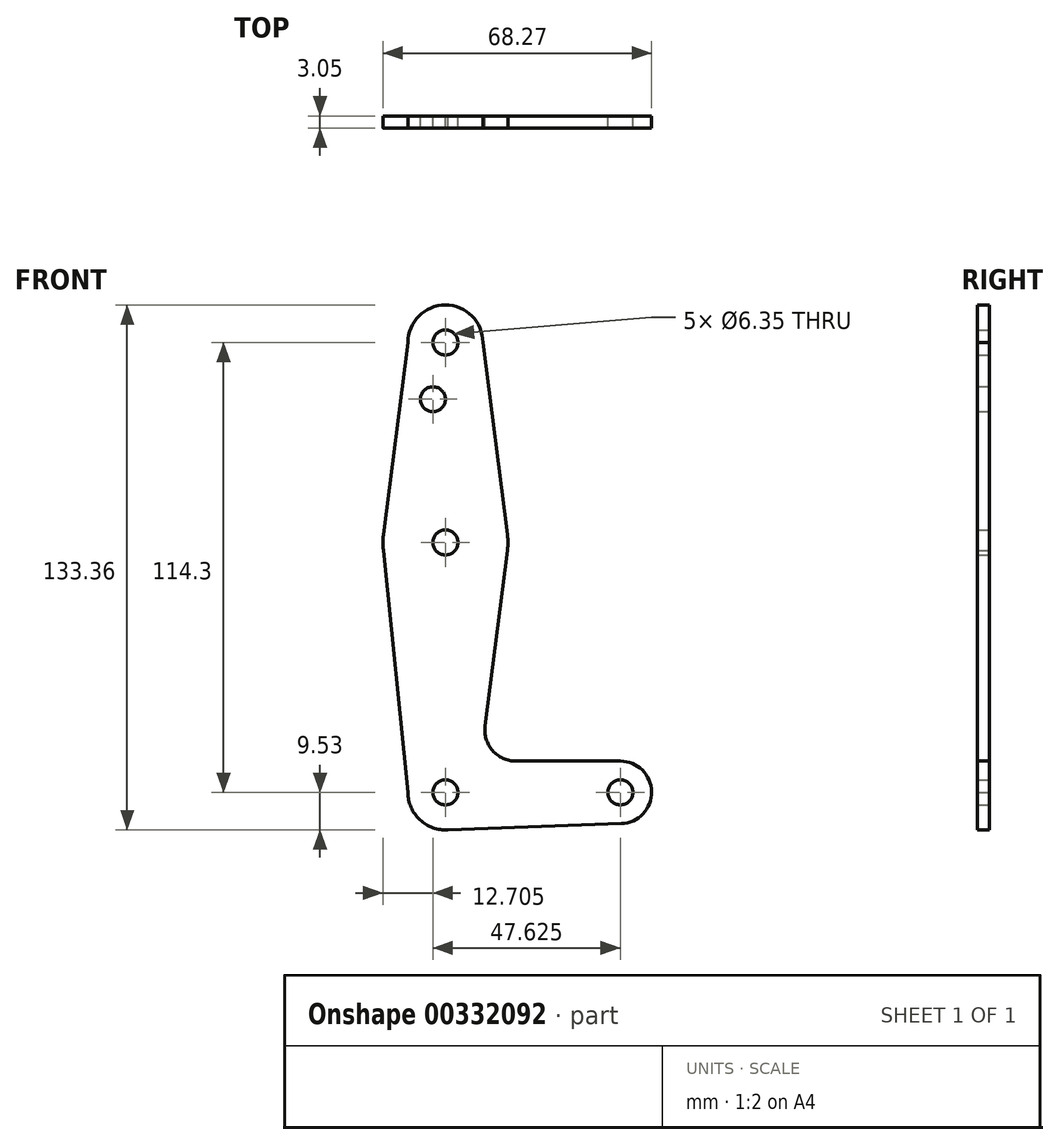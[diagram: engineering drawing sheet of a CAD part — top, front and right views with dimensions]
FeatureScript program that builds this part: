
annotation { "Feature Type Name" : "Feature", "Feature Type Description" : "" }
export const myFeature = defineFeature(function(context is Context, id is Id, definition is map)
    precondition{}
    {
        {
            var Q0;
            Q0=qCreatedBy(makeId("Front.planeOp"),FACE);
            var sketch = newSketch(context, id + "F0", { "sketchPlane" : qUnion([Q0])});
            skCircle(sketch, "E0", {"center": v(0, 0) * mm, "radius": 9.53 * mm});
            skCircle(sketch, "E1", {"center": v(44.45, 0) * mm, "radius": 7.94 * mm});
            skCircle(sketch, "E2", {"center": v(0, 114.3) * mm, "radius": 9.53 * mm});
            skCircle(sketch, "E3", {"center": v(0, 63.5) * mm, "radius": 15.88 * mm});
            skLineSegment(sketch, "E4", {"start": v(0, 114.3) * mm, "end": v(0, 114.3) * mm});
            skLineSegment(sketch, "E5", {"start": v(0, -9.52) * mm, "end": v(44.73, -7.93) * mm});
            skLineSegment(sketch, "E6", {"start": v(0, 0) * mm, "end": v(0, 114.3) * mm, "construction": true});
            skLineSegment(sketch, "E7", {"start": v(-9.53, 114.3) * mm, "end": v(-15.75, 65.5) * mm});
            skLineSegment(sketch, "E8", {"start": v(9.52, 114.3) * mm, "end": v(15.75, 65.5) * mm});
            skCircle(sketch, "E9", {"center": v(0, 63.5) * mm, "radius": 3.18 * mm});
            skCircle(sketch, "E10", {"center": v(-3.18, 99.89) * mm, "radius": 3.18 * mm});
            skCircle(sketch, "E11", {"center": v(0, 114.3) * mm, "radius": 3.18 * mm});
            skCircle(sketch, "E12", {"center": v(0, 0) * mm, "radius": 3.18 * mm});
            skCircle(sketch, "E13", {"center": v(44.45, 0) * mm, "radius": 3.18 * mm});
            skLineSegment(sketch, "E14", {"start": v(0, 0) * mm, "end": v(44.45, 0) * mm, "construction": true});
            skLineSegment(sketch, "E15", {"start": v(-9.52, 0) * mm, "end": v(-15.75, 61.5) * mm});
            skLineSegment(sketch, "E16", {"start": v(10.06, 16.9) * mm, "end": v(15.75, 61.5) * mm});
            skLineSegment(sketch, "E17", {"start": v(17.95, 7.94) * mm, "end": v(44.45, 7.94) * mm});
            skArc(sketch, "E18.filletArc", {"start": v(10.06, 16.9) * mm, "mid": v(11.98, 10.63) * mm, "end": v(17.95, 7.94) * mm});
            skSolve(sketch);
        }
        {
            var Q0;
            Q0 = qSketchRegion(id + "F0", true);
            extrude(context, id + "F1", {"entities" : qUnion([Q0]), "depth" : 3.05 * mm});
        }
    });
